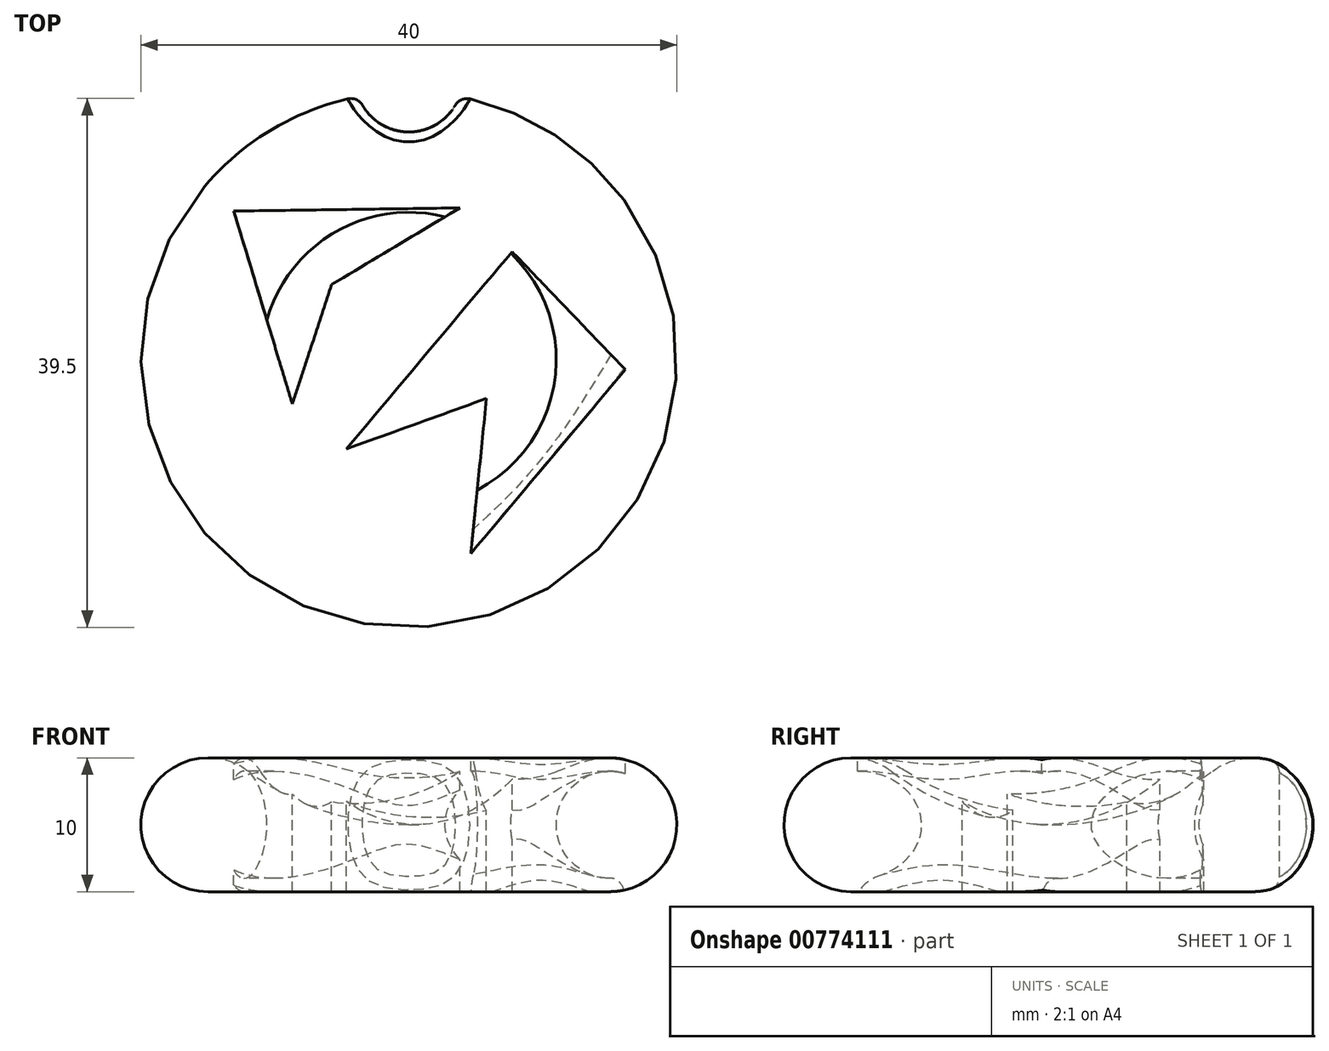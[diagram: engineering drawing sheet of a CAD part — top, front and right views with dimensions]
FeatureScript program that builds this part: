
annotation { "Feature Type Name" : "Feature", "Feature Type Description" : "" }
export const myFeature = defineFeature(function(context is Context, id is Id, definition is map)
    precondition{}
    {
        {
            var Q0;
            Q0=qCreatedBy(makeId("Front.planeOp"),FACE);
            var sketch = newSketch(context, id + "F0", { "sketchPlane" : qUnion([Q0])});
            skLineSegment(sketch, "E0", {"start": v(0, -20) * mm, "end": v(0, -25) * mm});
            skArc(sketch, "E1", {"start": v(-12, -16) * mm, "mid": v(-6.32, -18.97) * mm, "end": v(0, -20) * mm});
            skArc(sketch, "E2", {"start": v(-12, -16) * mm, "mid": v(-19.74, -18.42) * mm, "end": v(-15, -25) * mm});
            skLineSegment(sketch, "E3", {"start": v(0, -25) * mm, "end": v(-15, -25) * mm});
            skSolve(sketch);
        }
        {
            var Q0;
            Q0=makeQuery(id+"F0.imprint","IMPRINT",FACE,{"disambiguationData":[TD([[makeQuery(id+"F0.imprint","IMPRINT",EDGE,{"derivedFrom":sQuery(id+"F0.wireOp",EDGE,"E0")}),-1.0]])]});
            var Q1;
            Q1=sQuery(id+"F0.wireOp",EDGE,"E0");
            revolve(context, id + "F1", {"surfaceOperationType" : NewSurfaceOperationType.NEW, "entities" : qUnion([Q0]), "axis" : qUnion([Q1]), "revolveType" : RevolveType.FULL});
        }
        {
            var Q0;
            Q0=qCreatedBy(makeId("Top.planeOp"),FACE);
            var sketch = newSketch(context, id + "F2", { "sketchPlane" : qUnion([Q0])});
            skLineSegment(sketch, "E4", {"start": v(3.82, 11.33) * mm, "end": v(-13.07, 11.1) * mm});
            skLineSegment(sketch, "E5", {"start": v(-13.07, 11.1) * mm, "end": v(-8.7, -3.32) * mm});
            skLineSegment(sketch, "E6", {"start": v(3.82, 11.33) * mm, "end": v(-5.77, 5.6) * mm});
            skLineSegment(sketch, "E7", {"start": v(-5.77, 5.6) * mm, "end": v(-8.7, -3.32) * mm});
            skLineSegment(sketch, "E8", {"start": v(7.7, 8.07) * mm, "end": v(-4.68, -6.7) * mm});
            skLineSegment(sketch, "E9", {"start": v(-4.68, -6.7) * mm, "end": v(5.8, -2.9) * mm});
            skPoint(sketch, "E9.endSnap0", {"position": v(1.52, 0.69) * mm});
            skLineSegment(sketch, "E10", {"start": v(5.8, -2.9) * mm, "end": v(4.62, -14.5) * mm});
            skLineSegment(sketch, "E11", {"start": v(4.62, -14.5) * mm, "end": v(16.16, -0.75) * mm});
            skLineSegment(sketch, "E12", {"start": v(16.16, -0.75) * mm, "end": v(7.7, 8.07) * mm});
            skLineSegment(sketch, "E13.0", {"start": v(-8.7, -3.32) * mm, "end": v(4.62, -14.5) * mm, "construction": true});
            skLineSegment(sketch, "E14.0", {"start": v(1.52, 0.69) * mm, "end": v(5.8, -2.9) * mm, "construction": true});
            skLineSegment(sketch, "E15.0", {"start": v(3.82, 11.33) * mm, "end": v(7.7, 8.07) * mm, "construction": true});
            skSolve(sketch);
        }
        {
            var Q0;
            Q0 = qSketchRegion(id + "F2", true);
            extrude(context, id + "F3", {"entities" : qUnion([Q0]), "operationType" : NewBodyOperationType.REMOVE, "oppositeDirection" : true, "depth" : 25 * mm, "offsetDistance" : 25 * mm});
        }
        {
            var Q0;
            Q0=qCreatedBy(makeId("Front.planeOp"),FACE);
            var sketch = newSketch(context, id + "F4", { "sketchPlane" : qUnion([Q0])});
            skCircle(sketch, "E16", {"center": v(-15, -20) * mm, "radius": 4 * mm});
            skSolve(sketch);
        }
        {
            var Q0;
            Q0 = qSketchRegion(id + "F4", true);
            var Q1;
            Q1=sQuery(id+"F0.wireOp",EDGE,"E0");
            revolve(context, id + "F5", {"operationType" : NewBodyOperationType.ADD, "surfaceOperationType" : NewSurfaceOperationType.NEW, "entities" : qUnion([Q0]), "axis" : qUnion([Q1]), "revolveType" : RevolveType.FULL});
        }
        {
            var Q0;
            Q0=qCreatedBy(makeId("Top.planeOp"),FACE);
            var sketch = newSketch(context, id + "F6", { "sketchPlane" : qUnion([Q0])});
            skCircle(sketch, "E17", {"center": v(0, 21) * mm, "radius": 4 * mm});
            skSolve(sketch);
        }
        {
            var Q0;
            Q0 = qSketchRegion(id + "F6", true);
            extrude(context, id + "F7", {"entities" : qUnion([Q0]), "operationType" : NewBodyOperationType.REMOVE, "oppositeDirection" : true, "depth" : 25 * mm, "offsetDistance" : 25 * mm});
        }
        {
            var Q0;
            Q0=makeQuery(id+"F7.boolean.opBoolean","INTERSECT",EDGE,{"derivedFrom":[makeQuery(id+"F1.opRevolve","SWEPT_FACE",FACE,{"disambiguationData":[OSD([sQuery(id+"F0.wireOp",EDGE,"E2")])]}),makeQuery(id+"F7.opExtrude","SWEPT_FACE",FACE,{"disambiguationData":[OSD([sQuery(id+"F6.wireOp",EDGE,"E17")])]})]});
            fillet(context, id + "F8", {"entities" : qUnion([Q0]), "radius" : 1 * mm, "tangentPropagation" : true, "allowEdgeOverflow" : false});
        }
        {
            var Q0;
            Q0=makeQuery(id+"F5.boolean.opBoolean","INTERSECT",EDGE,{"disambiguationData":[OD(0.0)],"derivedFrom":[makeQuery(id+"F3.boolean.opBoolean","COPY",FACE,{"derivedFrom":makeQuery(id+"F3.opExtrude","SWEPT_FACE",FACE,{"disambiguationData":[OSD([sQuery(id+"F2.wireOp",EDGE,"E11")])]})}),makeQuery(id+"F5.opRevolve","SWEPT_FACE",FACE,{"disambiguationData":[OSD([sQuery(id+"F4.wireOp",EDGE,"E16")])]})]});
            fillet(context, id + "F9", {"entities" : qUnion([Q0]), "radius" : 1.5 * mm, "tangentPropagation" : true, "allowEdgeOverflow" : false});
        }
    });
